# Revit family: Maxlogic Détecteur
name_source: partatom
category: Fire Alarm Devices
units: mm (PartAtom-declared; Revit-internal decimal feet)

## family parameters
Cut with Voids When Loaded = No
Host = Face
Maintain Annotation Orientation = Yes
OmniClass Number = 23.85.30.21
OmniClass Title = Environmental Detection/Registration
Part Type = Normal
Room Calculation Point = No
Round Connector Dimension = Use Diameter
Shared = No

## types (10) — shared parameters
Adresse ligne 1 = Şerifali Mahallesi Kutup Sokak No:27/1-2-4 Ümraniye TR-34775 İSTANBUL
Boîtier de montage en surface étanche = ML-0121
Couleur = Blanc
Deuxime Matèriel = Plastique
Durée de la garantie Travail = 2
Durée de la garantie réservé = 2
Hauteur Nominale = 106 mm
Largeur Nominale = 51 mm
Longeur Nominale = 106 mm
Manuel d'installation = https://mavilielektronik.com
Manufacturer = Mavili Elektronik Ticaret A.Ş.
Model = Maxlogic
Numèro de Fax = (+)90 216 466 45 10
Socle montage de Surlévé = ML-0150
Socles Compatible = ML-0140
Socles Compatible 2 = ML-0141
Tempèrature de Fonctionnement = (-10°C) - (+50°C)
URL = https://www.mavili.com.tr
Voltage de fonctionnement (default) = 26 V/DC
zero-valued in all types: Cost, Default Elevation

## per-type parameters (varying)
| type | Cercle Chaleur | Cercle Multi critère | Charger adresse d'appareil | Code de  Performance | Code de Produit | Description | Détection de Radius | Matériel Principe | Numéro de pose des travaux publics | Poids | Sortie d'indicateur | Surface de Montage | Unité de durée de garantie | voltage fonction d'opération |
| Maxlogic Détecteur de fumée optique Conventionnelle | No | No |  | EN 54-7 | ML-2110 | Détecteur de Fumée optique Conventionnelle | 6,2 m | Plastique Blanche PC/ABS | 832-106 | 140 gr | MG-4000 | Montage à Mur | Year | 10-30V/DC |
| Maxlogic Détecteur de Fumée optique adressable Intelligent | No | No | Appareil d'addressage à Main | EN 54-7 | ML-1110 | Détecteur de Fumée optique adressable Intelligent | 6,2 m | Plastique Blanche PC/ABS | 833-500 | 100 gr | MG-4000.A | Montage à Mur | Ans | 18-33V/DC |
| Maxlogic Détecteur de fumée optique adresable , Isolateur de Court-Circuit | No | No | Appareil d'adressage à main | EN 54-7 / EN 54-17 | ML-1110.SCI | Détecteur de fumée optique adresable , Isolateur de Court-Circuit | 6,2 m | Plastique Rouge  PC/ABS | 833-501 | 100 gr | MG-4000.A | Montage à Plafond | Ans | 18-33V/DC |
| Maxlogic Détecteur de Chaleur Fixe Conventionnelle | Yes | No |  | EN 54-5 | ML-2120 | Détecteur de Chaleur Fixe Conventionnelle | 4,5 m | Plastique Rouge PC/ABS | 832-102 | 135 gr | MG-4000 | Montage à Mur | Ans | 10-30V/DC |
| Maxlogic Détecteur de Chaleur Conventionnelle | Yes | No |  | EN 54-5 | ML-2130 | Détecteur de chaleur Combiné | 4,5 m | Plastique Blanche PC/ABS | 832-103 | 135 gr | MG-4000 | Montage à Plafond | Year | 10-30V/DC |
| Maxlogic Détecteur de Chaleur Adressable | Yes | No | Appareil d'adressage à main | EN 54-5 | ML-1130 | Détecteur de Chaleur Adressable | 4,5 m | Plastique Blanche PC/ABS | 833-520 | 95 gr | MG-4000.A | Montage à plafond | Ans | 18-33V/DC |
| Maxlogic Détecteur de Chaleur adressable Intelligent ,Isolateur de Court-Circuit | Yes | No | Appareil d'adressage à main | EN 54-5 / EN 54-17 | ML-1130.SCI | Détecteur de Chaleur Adressable Intelligent | 4,5 m | Plastique Blanche PC/ABS | 833-521 | 95 gr | MG-4000.A | Montage à Plafond | Ans | 18-33V/DC |
| Maxlogic Détecteur de multi critère Conventionnelle | Yes | Yes |  | EN 54-5 / EN 54-7 | ML-2140 | Détecteur de multi critère Conventionnelle | 4,5 m | Plastique Blanche PC/ABS | 832-109 | 141 gr | MG-4000 | Montage à Plafond | Ans | 10-30V/DC |
| Maxlogic Détecteur de Multi Critère Adressable Intelligent | Yes | Yes | Appareil d'adressage à Main | EN 54-5 / EN 54-7 / EN 54-17 | ML-1140 | Détecteur de Multi Critère Adressable Intelligent | 4,5 m | Plastique Blanche PC/ABS | 833-530 | 100 gr | MG-4000.A | Montage à Plafond | Year | 18-33V/DC |
| Maxlogic Détecteur de Multi Critère Adressable Intelligent,Isolateur de Court-Circuit | Yes | Yes | Appareil d'adressage à main | EN 54-5 / EN 54-7 / EN 54-17 | ML-1140.SCI | Détecteur de Multi Critère Adressable Intelligent,Isolateur de Court-Circuit | 4,5 m | Plastique Blanche PC/ABS | 833-531 | 100 gr | MG-4000.A | Montage à Plafond | Ans | 18-33V/DC |

## geometry (parser evidence)
native form markers: Sweep x1
no freeform markers — native parametric forms only
